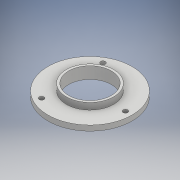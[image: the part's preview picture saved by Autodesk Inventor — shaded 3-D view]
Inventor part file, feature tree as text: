
AUTODESK INVENTOR PART (.ipt)
format: ipt  version: 2018 (Build 220112000, 112)  size: 136,704 bytes
history: native  units: mm
features: other x3, extrude x3, sketch x1
ambient origin geometry x8: Origin, YZ Plane, XZ Plane, XY Plane, X Axis, Y Axis, Z Axis, Center Point
bodies: Solid1 (feature_tree)
feature tree (7):
  other  "Table"
  other  "ACO.RODA15-01"
  other  "ACO.RODA15-02"
  extrude  "Extrusion1"  Depth=4.0mm TaperAngle=0.0deg
  extrude  "Extrusion2"  Depth=9.0mm TaperAngle=0.0deg
  extrude  "Extrusion3"  Depth=9.0mm
  sketch  "Sketch2"  dims[d0=32.5mm d3=4.0mm d4=0.0mm d5=9.0mm d6=0.0mm d8=3.6mm d9=27.0mm d10=30.0mm d12=360.0deg d14=6.0mm d15=0.0mm d16=64.0mm d21=36.0mm]
